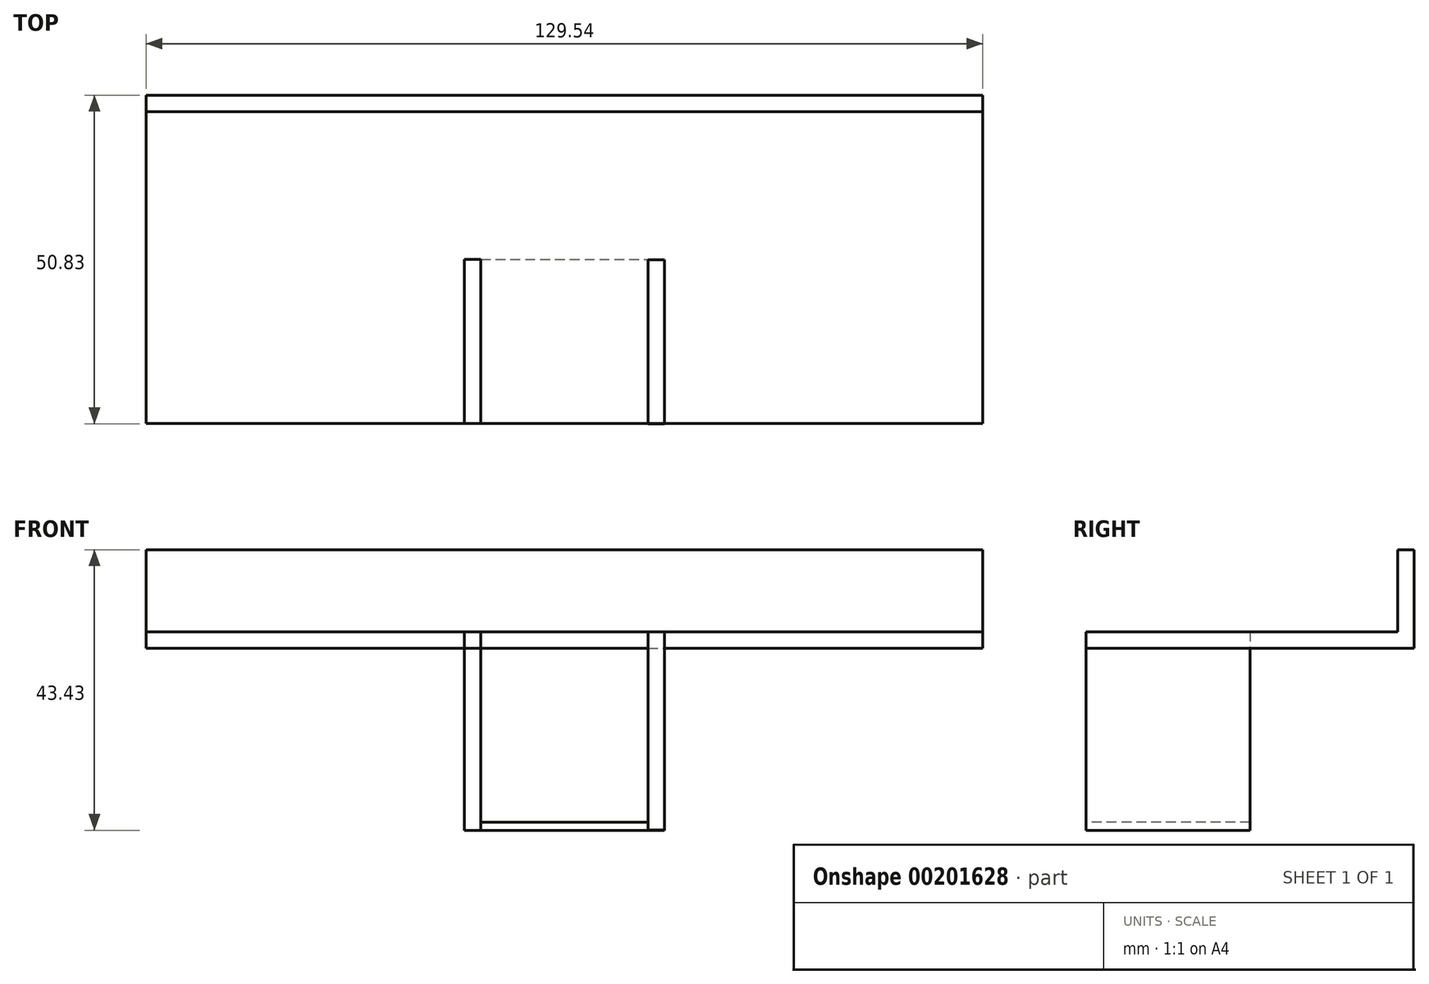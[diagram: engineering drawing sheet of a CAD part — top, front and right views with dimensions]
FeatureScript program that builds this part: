
annotation { "Feature Type Name" : "Feature", "Feature Type Description" : "" }
export const myFeature = defineFeature(function(context is Context, id is Id, definition is map)
    precondition{}
    {
        {
            var Q0;
            Q0=qCreatedBy(makeId("Top.planeOp"),FACE);
            var sketch = newSketch(context, id + "F0", { "sketchPlane" : qUnion([Q0])});
            skPoint(sketch, "E0.middle", {"position": v(0, 0) * mm});
            skLineSegment(sketch, "E1", {"start": v(0, 0) * mm, "end": v(-64.77, 0) * mm});
            skLineSegment(sketch, "E2", {"start": v(-64.77, 0) * mm, "end": v(-64.77, -12.7) * mm});
            skLineSegment(sketch, "E3", {"start": v(-64.77, -12.7) * mm, "end": v(64.77, -12.7) * mm});
            skLineSegment(sketch, "E4", {"start": v(-64.77, 0) * mm, "end": v(-64.77, 38.1) * mm});
            skLineSegment(sketch, "E5", {"start": v(-64.77, 38.1) * mm, "end": v(64.77, 38.1) * mm});
            skLineSegment(sketch, "E6", {"start": v(64.77, 38.1) * mm, "end": v(64.77, -12.7) * mm});
            skSolve(sketch);
        }
        {
            var Q0;
            Q0=qCreatedBy(makeId("Front.planeOp"),FACE);
            cPlane(context, id + "F1", {"entities" : qUnion([Q0]), "cplaneType" : CPlaneType.OFFSET, "offset" : 38.1 * mm, "oppositeDirection" : true, "width" : 152.4 * mm, "height" : 152.4 * mm});
        }
        {
            var Q0;
            Q0=qCreatedBy(makeId("Top.planeOp"),FACE);
            cPlane(context, id + "F2", {"entities" : qUnion([Q0]), "cplaneType" : CPlaneType.OFFSET, "offset" : 28.2 * mm, "oppositeDirection" : true, "width" : 152.4 * mm, "height" : 152.4 * mm});
        }
        {
            var Q0;
            Q0=qCreatedBy(id+"F2.planeOp",FACE);
            var sketch = newSketch(context, id + "F3", { "sketchPlane" : qUnion([Q0])});
            skLineSegment(sketch, "E7", {"start": v(0, 0) * mm, "end": v(0, 12.7) * mm});
            skLineSegment(sketch, "E8", {"start": v(0, 12.7) * mm, "end": v(12.95, 12.7) * mm});
            skLineSegment(sketch, "E9", {"start": v(0, 12.7) * mm, "end": v(-12.95, 12.7) * mm});
            skLineSegment(sketch, "E10", {"start": v(0, 0) * mm, "end": v(0, -12.7) * mm});
            skLineSegment(sketch, "E11", {"start": v(-12.95, 12.7) * mm, "end": v(-12.95, -12.7) * mm});
            skLineSegment(sketch, "E12", {"start": v(-12.95, -12.7) * mm, "end": v(12.95, -12.7) * mm});
            skLineSegment(sketch, "E13", {"start": v(12.95, 12.7) * mm, "end": v(12.95, -12.7) * mm});
            skSolve(sketch);
        }
        {
            var Q0;
            Q0=qCreatedBy(makeId("Right.planeOp"),FACE);
            cPlane(context, id + "F4", {"entities" : qUnion([Q0]), "cplaneType" : CPlaneType.OFFSET, "offset" : 15.5 * mm, "width" : 152.4 * mm, "height" : 152.4 * mm});
        }
        {
            var Q0;
            Q0=qCreatedBy(id+"F4.planeOp",FACE);
            var sketch = newSketch(context, id + "F5", { "sketchPlane" : qUnion([Q0])});
            skLineSegment(sketch, "E14", {"start": v(-0.03, -28.2) * mm, "end": v(0, 0) * mm, "construction": true});
            skLineSegment(sketch, "E15", {"start": v(-12.73, 2.54) * mm, "end": v(12.67, 2.54) * mm});
            skLineSegment(sketch, "E16", {"start": v(-12.73, -28.18) * mm, "end": v(12.67, -28.2) * mm});
            skLineSegment(sketch, "E17", {"start": v(12.67, 2.54) * mm, "end": v(12.67, -28.2) * mm});
            skLineSegment(sketch, "E18", {"start": v(-12.73, 2.54) * mm, "end": v(-12.73, -28.18) * mm});
            skSolve(sketch);
        }
        {
            var Q0;
            Q0=qCreatedBy(makeId("Right.planeOp"),FACE);
            cPlane(context, id + "F6", {"entities" : qUnion([Q0]), "cplaneType" : CPlaneType.OFFSET, "offset" : 15.5 * mm, "oppositeDirection" : true, "width" : 152.4 * mm, "height" : 152.4 * mm});
        }
        {
            var Q0;
            Q0=qCreatedBy(id+"F6.planeOp",FACE);
            var sketch = newSketch(context, id + "F7", { "sketchPlane" : qUnion([Q0])});
            skLineSegment(sketch, "E19", {"start": v(15.24, -28.2) * mm, "end": v(15.22, -28.2) * mm});
            skLineSegment(sketch, "E20", {"start": v(0, 0) * mm, "end": v(0, 2.54) * mm});
            skLineSegment(sketch, "E21", {"start": v(0, 2.54) * mm, "end": v(12.7, 2.54) * mm});
            skLineSegment(sketch, "E22", {"start": v(-15.24, -28.2) * mm, "end": v(-15.13, -28.2) * mm});
            skLineSegment(sketch, "E23", {"start": v(12.7, 2.54) * mm, "end": v(12.7, -28.2) * mm});
            skLineSegment(sketch, "E24", {"start": v(0, 2.54) * mm, "end": v(-12.7, 2.54) * mm});
            skLineSegment(sketch, "E25", {"start": v(-12.7, 2.54) * mm, "end": v(-12.7, -28.2) * mm});
            skLineSegment(sketch, "E26", {"start": v(-12.7, -28.2) * mm, "end": v(12.7, -28.2) * mm});
            skSolve(sketch);
        }
        {
            var Q0;
            Q0 = qSketchRegion(id + "F3", true);
            var Q1;
            Q1=makeQuery(id+"F3.imprint","IMPRINT",FACE,{"disambiguationData":[TD([[makeQuery(id+"F3.imprint","IMPRINT",EDGE,{"derivedFrom":sQuery(id+"F3.wireOp",EDGE,"Xzg1F8dH-z2M4-0MTN-nNoZ-EoRokcTVDoy5")}),1.0]])]});
            extrude(context, id + "F8", {"entities" : qUnion([Q0, Q1]), "depth" : 1.27 * mm});
        }
        {
            var Q0;
            Q0 = qSketchRegion(id + "F7", true);
            extrude(context, id + "F9", {"entities" : qUnion([Q0]), "depth" : 2.54 * mm});
        }
        {
            var Q0;
            Q0 = qSketchRegion(id + "F5", true);
            extrude(context, id + "F10", {"entities" : qUnion([Q0]), "oppositeDirection" : true, "depth" : 2.54 * mm});
        }
        {
            var Q0;
            Q0 = qSketchRegion(id + "F0", true);
            extrude(context, id + "F11", {"entities" : qUnion([Q0]), "depth" : 2.54 * mm});
        }
        {
            var Q0;
            Q0=qCreatedBy(id+"F1.planeOp",FACE);
            var sketch = newSketch(context, id + "F12", { "sketchPlane" : qUnion([Q0])});
            skLineSegment(sketch, "E27", {"start": v(0, 0) * mm, "end": v(64.77, 0) * mm});
            skLineSegment(sketch, "E28", {"start": v(0, 0) * mm, "end": v(-64.77, 0) * mm});
            skLineSegment(sketch, "E29", {"start": v(64.77, 0) * mm, "end": v(64.77, 15.24) * mm});
            skLineSegment(sketch, "E30", {"start": v(-64.77, 0) * mm, "end": v(-64.77, 15.24) * mm});
            skLineSegment(sketch, "E31", {"start": v(64.77, 15.24) * mm, "end": v(-64.77, 15.24) * mm});
            skSolve(sketch);
        }
        {
            var Q0;
            Q0=makeQuery(id+"F12.imprint","IMPRINT",FACE,{"disambiguationData":[TD([[makeQuery(id+"F12.imprint","IMPRINT",EDGE,{"derivedFrom":sQuery(id+"F12.wireOp",EDGE,"E27")}),1.0]])]});
            extrude(context, id + "F13", {"entities" : qUnion([Q0]), "operationType" : NewBodyOperationType.ADD, "depth" : 2.54 * mm});
        }
    });
